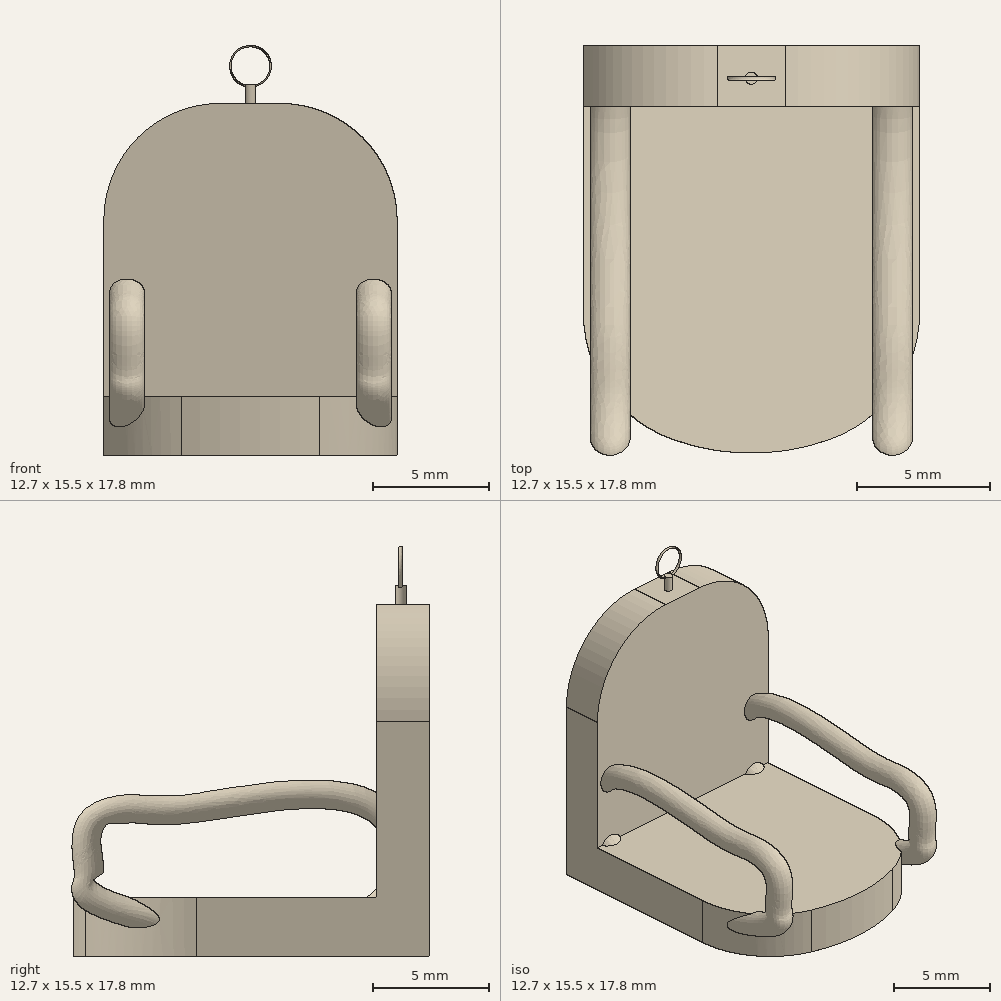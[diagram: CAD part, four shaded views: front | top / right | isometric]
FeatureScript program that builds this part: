
annotation { "Feature Type Name" : "Feature", "Feature Type Description" : "" }
export const myFeature = defineFeature(function(context is Context, id is Id, definition is map)
    precondition{}
    {
        {
            var Q0;
            Q0=qCreatedBy(makeId("Top.planeOp"),FACE);
            var sketch = newSketch(context, id + "F0", { "sketchPlane" : qUnion([Q0])});
            skLineSegment(sketch, "E0.bottom", {"start": v(-6.2, 2.1) * mm, "end": v(6.5, 2.1) * mm});
            skLineSegment(sketch, "E0.left", {"start": v(-6.2, 2.1) * mm, "end": v(-6.2, -10.6) * mm});
            skLineSegment(sketch, "E0.right", {"start": v(6.5, 2.1) * mm, "end": v(6.5, -10.6) * mm});
            skArc(sketch, "E1", {"start": v(-6.2, -10.6) * mm, "mid": v(0.14, -13.3) * mm, "end": v(6.5, -10.6) * mm});
            skSolve(sketch);
        }
        {
            var Q0;
            Q0=makeQuery(id+"F0.imprint","IMPRINT",FACE,{"disambiguationData":[TD([[makeQuery(id+"F0.imprint","IMPRINT",EDGE,{"derivedFrom":sQuery(id+"F0.wireOp",EDGE,"E0.bottom")}),-1.0]])]});
            extrude(context, id + "F1", {"entities" : qUnion([Q0]), "depth" : 2.54 * mm, "offsetDistance" : 25.4 * mm});
        }
        {
            var Q0;
            Q0=makeQuery(id+"F1.opExtrude","CAP_FACE",FACE,{"disambiguationData":[OSD([sQuery(id+"F0.wireOp",EDGE,"E0.bottom"),sQuery(id+"F0.wireOp",EDGE,"E0.left"),sQuery(id+"F0.wireOp",EDGE,"E0.right"),sQuery(id+"F0.wireOp",EDGE,"E1")])],"isStart":false});
            var sketch = newSketch(context, id + "F2", { "sketchPlane" : qUnion([Q0])});
            skLineSegment(sketch, "E2.bottom", {"start": v(-6.2, 2.1) * mm, "end": v(6.5, 2.1) * mm});
            skLineSegment(sketch, "E2.top", {"start": v(-6.2, -0.21) * mm, "end": v(6.5, -0.21) * mm});
            skLineSegment(sketch, "E2.left", {"start": v(-6.2, 2.1) * mm, "end": v(-6.2, -0.21) * mm});
            skLineSegment(sketch, "E2.right", {"start": v(6.5, 2.1) * mm, "end": v(6.5, -0.21) * mm});
            skSolve(sketch);
        }
        {
            var Q0;
            Q0=makeQuery(id+"F2.imprint","IMPRINT",FACE,{"disambiguationData":[TD([[makeQuery(id+"F2.imprint","IMPRINT",EDGE,{"derivedFrom":sQuery(id+"F2.wireOp",EDGE,"E2.bottom")}),-1.0]])]});
            extrude(context, id + "F3", {"entities" : qUnion([Q0]), "operationType" : NewBodyOperationType.ADD, "depth" : 12.7 * mm, "offsetDistance" : 25.4 * mm});
        }
        {
            var Q0;
            Q0=makeQuery(id+"F3.opExtrude","CAP_EDGE",EDGE,{"disambiguationData":[OSD([sQuery(id+"F2.wireOp",EDGE,"E2.left")])],"isStart":false});
            var Q1;
            Q1=makeQuery(id+"F3.opExtrude","CAP_EDGE",EDGE,{"disambiguationData":[OSD([sQuery(id+"F2.wireOp",EDGE,"E2.right")])],"isStart":false});
            var Q2;
            Q2=makeQuery(id+"F1.opExtrude","SWEPT_EDGE",EDGE,{"disambiguationData":[OSD([sQuery(id+"F0.wireOp",EDGE,"E0.right"),sQuery(id+"F0.wireOp",EDGE,"E1")])]});
            var Q3;
            Q3=makeQuery(id+"F1.opExtrude","SWEPT_EDGE",EDGE,{"disambiguationData":[OSD([sQuery(id+"F0.wireOp",EDGE,"E0.left"),sQuery(id+"F0.wireOp",EDGE,"E1")])]});
            fillet(context, id + "F4", {"entities" : qUnion([Q0, Q1, Q2, Q3]), "radius" : 5.08 * mm, "tangentPropagation" : true, "allowEdgeOverflow" : false});
        }
        {
            var Q0;
            Q0=makeQuery(id+"F3.opExtrude","SWEPT_FACE",FACE,{"disambiguationData":[OSD([sQuery(id+"F2.wireOp",EDGE,"E2.top")])]});
            var sketch = newSketch(context, id + "F5", { "sketchPlane" : qUnion([Q0])});
            skCircle(sketch, "E3", {"center": v(5.48, 6.35) * mm, "radius": 0.76 * mm});
            skPoint(sketch, "E3.centerSnap0", {"position": v(6.5, 6.35) * mm});
            skCircle(sketch, "E4", {"center": v(-5.2, 6.35) * mm, "radius": 0.76 * mm});
            skPoint(sketch, "E4.centerSnap0", {"position": v(-6.2, 6.35) * mm});
            skSolve(sketch);
        }
        {
            var Q0;
            Q0=makeQuery(id+"F3.boolean.opBoolean","MERGE",FACE,{"derivedFrom":[makeQuery(id+"F1.opExtrude","SWEPT_FACE",FACE,{"disambiguationData":[OSD([sQuery(id+"F0.wireOp",EDGE,"E0.right")])]}),makeQuery(id+"F3.opExtrude","SWEPT_FACE",FACE,{"disambiguationData":[OSD([sQuery(id+"F2.wireOp",EDGE,"E2.right")])]})]});
            cPlane(context, id + "F6", {"entities" : qUnion([Q0]), "cplaneType" : CPlaneType.OFFSET, "offset" : 1.02 * mm, "oppositeDirection" : true, "width" : 152.4 * mm, "height" : 152.4 * mm});
        }
        {
            var Q0;
            Q0=qCreatedBy(id+"F6.planeOp",FACE);
            var sketch = newSketch(context, id + "F7", { "sketchPlane" : qUnion([Q0])});
            skFitSpline(sketch, "E5", {"points": [v(-0.2, 6.43) * mm, v(-8.52, 6.44) * mm, v(-10.98, 6.43) * mm, v(-12.42, 5.9) * mm, v(-12.8, 4.72) * mm, v(-12.74, 3.51) * mm, v(-12.53, 2.55) * mm, v(-0.3, 2) * mm, v(-0.2, 6.43) * mm]});
            skSolve(sketch);
        }
        {
            var Q0;
            Q0 = qSketchRegion(id + "F5", true);
            var Q1;
            Q1=sQuery(id+"F7.wireOp",EDGE,"E5");
            sweep(context, id + "F8", {"operationType" : NewBodyOperationType.ADD, "profiles" : qUnion([Q0]), "path" : qUnion([Q1])});
        }
        {
            var Q0;
            Q0=makeQuery(id+"F3.opExtrude","CAP_FACE",FACE,{"disambiguationData":[OSD([sQuery(id+"F2.wireOp",EDGE,"E2.bottom"),sQuery(id+"F2.wireOp",EDGE,"E2.top"),sQuery(id+"F2.wireOp",EDGE,"E2.left"),sQuery(id+"F2.wireOp",EDGE,"E2.right")])],"isStart":false});
            var sketch = newSketch(context, id + "F9", { "sketchPlane" : qUnion([Q0])});
            skCircle(sketch, "E6", {"center": v(0.14, 0.85) * mm, "radius": 0.23 * mm});
            skPoint(sketch, "E6.centerSnap0", {"position": v(0.14, -0.21) * mm});
            skSolve(sketch);
        }
        {
            var Q0;
            Q0=makeQuery(id+"F9.imprint","IMPRINT",FACE,{"disambiguationData":[TD([[makeQuery(id+"F9.imprint","IMPRINT",EDGE,{"derivedFrom":sQuery(id+"F9.wireOp",EDGE,"E6")}),1.0]])]});
            extrude(context, id + "F10", {"entities" : qUnion([Q0]), "operationType" : NewBodyOperationType.ADD, "depth" : 0.81 * mm, "offsetDistance" : 25.4 * mm});
        }
        {
            var Q0;
            Q0=makeQuery(id+"F3.boolean.opBoolean","MERGE",FACE,{"derivedFrom":[makeQuery(id+"F1.opExtrude","SWEPT_FACE",FACE,{"disambiguationData":[OSD([sQuery(id+"F0.wireOp",EDGE,"E0.bottom")])]}),makeQuery(id+"F3.opExtrude","SWEPT_FACE",FACE,{"disambiguationData":[OSD([sQuery(id+"F2.wireOp",EDGE,"E2.bottom")])]})]});
            cPlane(context, id + "F11", {"entities" : qUnion([Q0]), "cplaneType" : CPlaneType.OFFSET, "offset" : 1.24 * mm, "oppositeDirection" : true, "width" : 152.4 * mm, "height" : 152.4 * mm});
        }
        {
            var Q0;
            Q0=qCreatedBy(id+"F11.planeOp",FACE);
            var sketch = newSketch(context, id + "F12", { "sketchPlane" : qUnion([Q0])});
            skCircle(sketch, "E7", {"center": v(-0.15, 16.84) * mm, "radius": 0.51 * mm});
            skSolve(sketch);
        }
        {
            var Q0;
            Q0=makeQuery(id+"F10.opExtrude","CAP_FACE",FACE,{"disambiguationData":[OSD([sQuery(id+"F9.wireOp",EDGE,"E6")])],"isStart":false});
            var sketch = newSketch(context, id + "F13", { "sketchPlane" : qUnion([Q0])});
            skCircle(sketch, "E8", {"center": v(0.5, 0.85) * mm, "radius": 0.08 * mm});
            skSolve(sketch);
        }
        {
            var Q0;
            Q0=makeQuery(id+"F13.imprint","IMPRINT",FACE,{"disambiguationData":[TD([[makeQuery(id+"F13.imprint","IMPRINT",EDGE,{"derivedFrom":sQuery(id+"F13.wireOp",EDGE,"E8")}),1.0]])]});
            var Q1;
            Q1=sQuery(id+"F12.wireOp",EDGE,"E7");
            sweep(context, id + "F14", {"operationType" : NewBodyOperationType.ADD, "profiles" : qUnion([Q0]), "path" : qUnion([Q1])});
        }
    });
